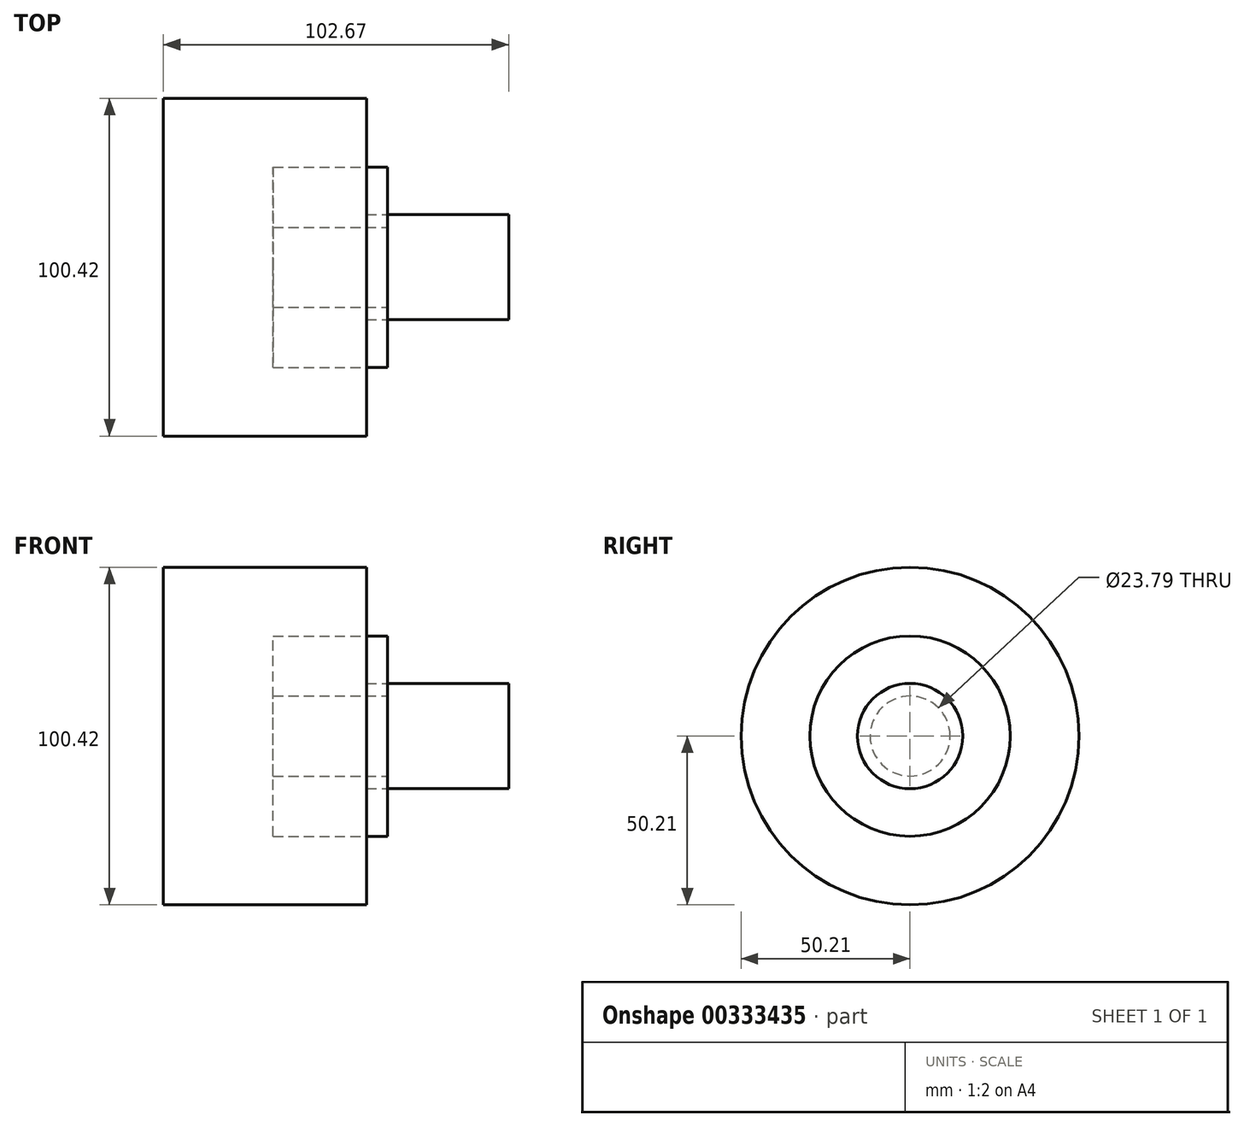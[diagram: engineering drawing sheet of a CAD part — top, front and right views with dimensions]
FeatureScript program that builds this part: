
annotation { "Feature Type Name" : "Feature", "Feature Type Description" : "" }
export const myFeature = defineFeature(function(context is Context, id is Id, definition is map)
    precondition{}
    {
        {
            var Q0;
            Q0=qCreatedBy(makeId("Front.planeOp"),FACE);
            var sketch = newSketch(context, id + "F0", { "sketchPlane" : qUnion([Q0])});
            skLineSegment(sketch, "E0.bottom", {"start": v(-6.27, 0) * mm, "end": v(-46.14, 0) * mm});
            skLineSegment(sketch, "E0.top", {"start": v(-6.27, 33.94) * mm, "end": v(-46.14, 33.94) * mm});
            skLineSegment(sketch, "E0.left", {"start": v(-6.27, 0) * mm, "end": v(-6.27, 33.94) * mm});
            skLineSegment(sketch, "E0.right", {"start": v(-46.14, 0) * mm, "end": v(-46.14, 33.94) * mm});
            skLineSegment(sketch, "E1.bottom", {"start": v(-27.77, -11.9) * mm, "end": v(6.26, -11.9) * mm});
            skLineSegment(sketch, "E1.top", {"start": v(-27.77, -29.78) * mm, "end": v(6.26, -29.78) * mm});
            skLineSegment(sketch, "E1.left", {"start": v(-27.77, -11.9) * mm, "end": v(-27.77, -29.78) * mm});
            skLineSegment(sketch, "E1.right", {"start": v(6.26, -11.9) * mm, "end": v(6.26, -29.78) * mm});
            skLineSegment(sketch, "E2", {"start": v(-60.35, 0) * mm, "end": v(-60.35, 50.2) * mm});
            skLineSegment(sketch, "E3", {"start": v(-60.35, 50.2) * mm, "end": v(0, 50.2) * mm});
            skLineSegment(sketch, "E4", {"start": v(0, 50.2) * mm, "end": v(0, 15.65) * mm});
            skLineSegment(sketch, "E5", {"start": v(0, 15.65) * mm, "end": v(42.32, 15.65) * mm});
            skLineSegment(sketch, "E6", {"start": v(42.32, 15.65) * mm, "end": v(42.32, 0) * mm});
            skLineSegment(sketch, "E7", {"start": v(42.32, 0) * mm, "end": v(-60.35, 0) * mm});
            skSolve(sketch);
        }
        {
            var Q0;
            Q0 = qSketchRegion(id + "F0", true);
            var Q1;
            Q1=sQuery(id+"F0.wireOp",EDGE,"E0.bottom");
            revolve(context, id + "F1", {"entities" : qUnion([Q0]), "axis" : qUnion([Q1]), "revolveType" : RevolveType.FULL});
        }
    });
